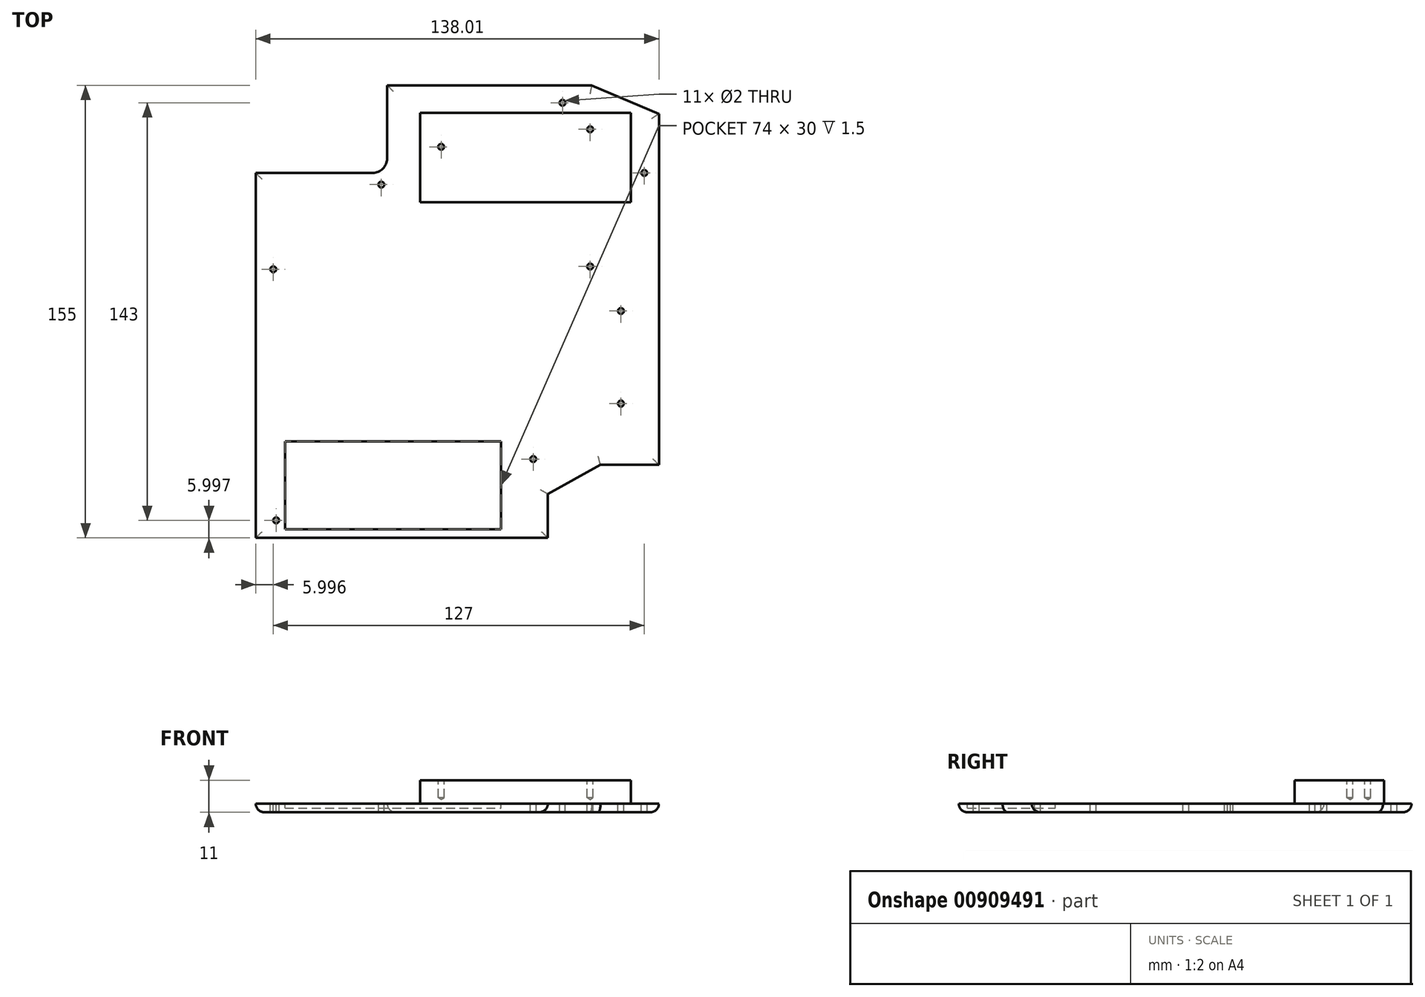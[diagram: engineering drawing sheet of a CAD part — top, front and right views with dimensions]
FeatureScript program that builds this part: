
annotation { "Feature Type Name" : "Feature", "Feature Type Description" : "" }
export const myFeature = defineFeature(function(context is Context, id is Id, definition is map)
    precondition{}
    {
        {
            var Q0;
            Q0=qCreatedBy(makeId("Top.planeOp"),FACE);
            var sketch = newSketch(context, id + "F0", { "sketchPlane" : qUnion([Q0])});
            skLineSegment(sketch, "E0.bottom", {"start": v(-71.65, 50.25) * mm, "end": v(-26.65, 50.25) * mm});
            skLineSegment(sketch, "E0.top", {"start": v(-71.65, -74.75) * mm, "end": v(-26.65, -74.75) * mm});
            skLineSegment(sketch, "E0.left", {"start": v(-71.65, 50.25) * mm, "end": v(-71.65, -74.75) * mm});
            skLineSegment(sketch, "E0.right", {"start": v(-26.65, 50.25) * mm, "end": v(-26.65, -74.75) * mm});
            skLineSegment(sketch, "E1.bottom", {"start": v(-26.65, 50.25) * mm, "end": v(43.35, 50.25) * mm});
            skLineSegment(sketch, "E1.top", {"start": v(-26.65, 80.25) * mm, "end": v(43.35, 80.25) * mm});
            skLineSegment(sketch, "E1.left", {"start": v(-26.65, 50.25) * mm, "end": v(-26.65, 80.25) * mm});
            skLineSegment(sketch, "E1.right", {"start": v(43.35, 50.25) * mm, "end": v(43.35, 80.25) * mm});
            skLineSegment(sketch, "E2", {"start": v(43.35, 80.25) * mm, "end": v(66.36, 70.48) * mm});
            skLineSegment(sketch, "E3.bottom", {"start": v(66.36, 70.48) * mm, "end": v(43.35, 70.48) * mm});
            skLineSegment(sketch, "E3.top", {"start": v(66.36, 50.25) * mm, "end": v(43.35, 50.25) * mm});
            skLineSegment(sketch, "E3.left", {"start": v(66.36, 70.48) * mm, "end": v(66.36, 50.25) * mm});
            skLineSegment(sketch, "E3.right", {"start": v(43.35, 70.48) * mm, "end": v(43.35, 50.25) * mm});
            skLineSegment(sketch, "E4.bottom", {"start": v(66.36, 50.25) * mm, "end": v(46.36, 50.25) * mm});
            skLineSegment(sketch, "E4.top", {"start": v(66.36, -49.75) * mm, "end": v(46.36, -49.75) * mm});
            skLineSegment(sketch, "E4.left", {"start": v(66.36, 50.25) * mm, "end": v(66.36, -49.75) * mm});
            skLineSegment(sketch, "E4.right", {"start": v(46.36, 50.25) * mm, "end": v(46.36, -49.75) * mm});
            skLineSegment(sketch, "E5.bottom", {"start": v(-71.65, -74.75) * mm, "end": v(28.35, -74.75) * mm});
            skLineSegment(sketch, "E5.top", {"start": v(-71.65, -59.75) * mm, "end": v(28.35, -59.75) * mm});
            skLineSegment(sketch, "E5.left", {"start": v(-71.65, -74.75) * mm, "end": v(-71.65, -59.75) * mm});
            skLineSegment(sketch, "E5.right", {"start": v(28.35, -74.75) * mm, "end": v(28.35, -59.75) * mm});
            skLineSegment(sketch, "E6", {"start": v(28.35, -59.75) * mm, "end": v(46.36, -49.75) * mm});
            skSolve(sketch);
        }
        {
            var Q0;
            {var subQ0=sQuery(id+"F0.wireOp",EDGE,"E0.bottom");Q0=makeQuery(id+"F0.imprint","IMPRINT",FACE,{"disambiguationData":[TD([[makeQuery(id+"F0.imprint","IMPRINT",EDGE,{"derivedFrom":subQ0}),-1.0]])]});}
            var Q1;
            {var subQ1=sQuery(id+"F0.wireOp",EDGE,"E1.bottom");Q1=makeQuery(id+"F0.imprint","IMPRINT",FACE,{"disambiguationData":[TD([[makeQuery(id+"F0.imprint","IMPRINT",EDGE,{"derivedFrom":subQ1}),-1.0]])]});}
            var Q2;
            {var subQ0=sQuery(id+"F0.wireOp",EDGE,"E0.top");Q2=makeQuery(id+"F0.imprint","IMPRINT",FACE,{"disambiguationData":[TD([[makeQuery(id+"F0.imprint","IMPRINT",EDGE,{"derivedFrom":subQ0}),1.0]])]});}
            var Q3;
            Q3=makeQuery(id+"F0.imprint","IMPRINT",FACE,{"disambiguationData":[TD([[makeQuery(id+"F0.imprint","IMPRINT",EDGE,{"derivedFrom":sQuery(id+"F0.wireOp",EDGE,"E4.top")}),-1.0]])]});
            var Q4;
            {var subQ0=sQuery(id+"F0.wireOp",EDGE,"E5.bottom");Q4=makeQuery(id+"F0.imprint","IMPRINT",FACE,{"disambiguationData":[TD([[makeQuery(id+"F0.imprint","IMPRINT",EDGE,{"derivedFrom":subQ0}),1.0]])]});}
            var Q5;
            {var subQ1=sQuery(id+"F0.wireOp",EDGE,"E1.bottom");Q5=makeQuery(id+"F0.imprint","IMPRINT",FACE,{"disambiguationData":[TD([[makeQuery(id+"F0.imprint","IMPRINT",EDGE,{"derivedFrom":subQ1}),1.0]])]});}
            var Q6;
            {var subQ3=sQuery(id+"F0.wireOp",EDGE,"E3.bottom");Q6=makeQuery(id+"F0.imprint","IMPRINT",FACE,{"disambiguationData":[TD([[makeQuery(id+"F0.imprint","IMPRINT",EDGE,{"derivedFrom":subQ3}),1.0]])]});}
            var Q7;
            {var subQ0=sQuery(id+"F0.wireOp",EDGE,"E2");Q7=makeQuery(id+"F0.imprint","IMPRINT",FACE,{"disambiguationData":[TD([[makeQuery(id+"F0.imprint","IMPRINT",EDGE,{"derivedFrom":subQ0}),-1.0]])]});}
            extrude(context, id + "F1", {"entities" : qUnion([Q0, Q1, Q2, Q3, Q4, Q5, Q6, Q7]), "depth" : 3 * mm, "offsetDistance" : 25 * mm});
        }
        {
            var Q0;
            Q0=makeQuery(id+"F1.opExtrude","SWEPT_EDGE",EDGE,{"disambiguationData":[OSD([sQuery(id+"F0.wireOp",EDGE,"E0.bottom"),sQuery(id+"F0.wireOp",EDGE,"E0.right"),sQuery(id+"F0.wireOp",EDGE,"E1.bottom"),sQuery(id+"F0.wireOp",EDGE,"E1.left")])]});
            fillet(context, id + "F2", {"entities" : qUnion([Q0]), "radius" : 5 * mm, "tangentPropagation" : true, "allowEdgeOverflow" : false});
        }
        {
            var Q0;
            Q0=makeQuery(id+"F1.opExtrude","CAP_FACE",FACE,{"disambiguationData":[OSD([sQuery(id+"F0.wireOp",EDGE,"E0.bottom"),sQuery(id+"F0.wireOp",EDGE,"E0.top"),sQuery(id+"F0.wireOp",EDGE,"E0.left"),sQuery(id+"F0.wireOp",EDGE,"E1.top"),sQuery(id+"F0.wireOp",EDGE,"E1.left"),sQuery(id+"F0.wireOp",EDGE,"E2"),sQuery(id+"F0.wireOp",EDGE,"E3.left"),sQuery(id+"F0.wireOp",EDGE,"E4.top"),sQuery(id+"F0.wireOp",EDGE,"E4.left"),sQuery(id+"F0.wireOp",EDGE,"E5.bottom"),sQuery(id+"F0.wireOp",EDGE,"E5.right"),sQuery(id+"F0.wireOp",EDGE,"E6")])],"isStart":true});
            fillet(context, id + "F3", {"entities" : qUnion([Q0]), "radius" : 3 * mm, "tangentPropagation" : true, "allowEdgeOverflow" : false});
        }
        {
            var Q0;
            Q0=makeQuery(id+"F1.opExtrude","CAP_FACE",FACE,{"disambiguationData":[OSD([sQuery(id+"F0.wireOp",EDGE,"E0.bottom"),sQuery(id+"F0.wireOp",EDGE,"E0.top"),sQuery(id+"F0.wireOp",EDGE,"E0.left"),sQuery(id+"F0.wireOp",EDGE,"E1.top"),sQuery(id+"F0.wireOp",EDGE,"E1.left"),sQuery(id+"F0.wireOp",EDGE,"E2"),sQuery(id+"F0.wireOp",EDGE,"E3.left"),sQuery(id+"F0.wireOp",EDGE,"E4.top"),sQuery(id+"F0.wireOp",EDGE,"E4.left"),sQuery(id+"F0.wireOp",EDGE,"E5.bottom"),sQuery(id+"F0.wireOp",EDGE,"E5.right"),sQuery(id+"F0.wireOp",EDGE,"E6")])],"isStart":false});
            var sketch = newSketch(context, id + "F4", { "sketchPlane" : qUnion([Q0])});
            skPoint(sketch, "E7", {"position": v(-64.65, -68.75) * mm});
            skPoint(sketch, "E8", {"position": v(-65.65, 17.25) * mm});
            skPoint(sketch, "E9", {"position": v(-28.65, 46.25) * mm});
            skPoint(sketch, "E10", {"position": v(33.35, 74.25) * mm});
            skPoint(sketch, "E11", {"position": v(61.35, 50.25) * mm});
            skPoint(sketch, "E12", {"position": v(23.35, -47.75) * mm});
            skPoint(sketch, "E13", {"position": v(53.36, -28.75) * mm});
            skPoint(sketch, "E14", {"position": v(53.36, 2.97) * mm});
            skSolve(sketch);
        }
        {
            var Q0;
            Q0=sQuery(id+"F4.wireOp",VERTEX,"E8");
            var Q1;
            Q1=sQuery(id+"F4.wireOp",VERTEX,"E7");
            var Q2;
            Q2=sQuery(id+"F4.wireOp",VERTEX,"E12");
            var Q3;
            Q3=sQuery(id+"F4.wireOp",VERTEX,"E13");
            var Q4;
            Q4=sQuery(id+"F4.wireOp",VERTEX,"E14");
            var Q5;
            Q5=sQuery(id+"F4.wireOp",VERTEX,"E11");
            var Q6;
            Q6=sQuery(id+"F4.wireOp",VERTEX,"E10");
            var Q7;
            Q7=sQuery(id+"F4.wireOp",VERTEX,"E9");
            var Q8;
            Q8=makeQuery(id+"F1.opExtrude","SWEPT_BODY",BODY,{"disambiguationData":[OSD([sQuery(id+"F0.wireOp",EDGE,"E0.bottom"),sQuery(id+"F0.wireOp",EDGE,"E0.top"),sQuery(id+"F0.wireOp",EDGE,"E0.left"),sQuery(id+"F0.wireOp",EDGE,"E1.top"),sQuery(id+"F0.wireOp",EDGE,"E1.left"),sQuery(id+"F0.wireOp",EDGE,"E2"),sQuery(id+"F0.wireOp",EDGE,"E3.left"),sQuery(id+"F0.wireOp",EDGE,"E4.top"),sQuery(id+"F0.wireOp",EDGE,"E4.left"),sQuery(id+"F0.wireOp",EDGE,"E5.bottom"),sQuery(id+"F0.wireOp",EDGE,"E5.right"),sQuery(id+"F0.wireOp",EDGE,"E6")])]});
            hole(context, id + "F5", {"style" : HoleStyle.SIMPLE, "endStyle" : HoleEndStyle.THROUGH, "holeDiameter" : 2 * mm, "majorDiameter" : 5 * mm, "isTappedThrough" : true, "tappedDepth" : 12 * mm, "tapClearance" : 3, "locations" : qUnion([Q0, Q1, Q2, Q3, Q4, Q5, Q6, Q7]), "scope" : qUnion([Q8])});
        }
        {
            var Q0;
            Q0=makeQuery(id+"F1.opExtrude","CAP_FACE",FACE,{"disambiguationData":[OSD([sQuery(id+"F0.wireOp",EDGE,"E0.bottom"),sQuery(id+"F0.wireOp",EDGE,"E0.top"),sQuery(id+"F0.wireOp",EDGE,"E0.left"),sQuery(id+"F0.wireOp",EDGE,"E1.top"),sQuery(id+"F0.wireOp",EDGE,"E1.left"),sQuery(id+"F0.wireOp",EDGE,"E2"),sQuery(id+"F0.wireOp",EDGE,"E3.left"),sQuery(id+"F0.wireOp",EDGE,"E4.top"),sQuery(id+"F0.wireOp",EDGE,"E4.left"),sQuery(id+"F0.wireOp",EDGE,"E5.bottom"),sQuery(id+"F0.wireOp",EDGE,"E5.right"),sQuery(id+"F0.wireOp",EDGE,"E6")])],"isStart":false});
            var sketch = newSketch(context, id + "F6", { "sketchPlane" : qUnion([Q0])});
            skLineSegment(sketch, "E15.bottom", {"start": v(-61.65, -71.75) * mm, "end": v(12.35, -71.75) * mm});
            skLineSegment(sketch, "E15.top", {"start": v(-61.65, -41.75) * mm, "end": v(12.35, -41.75) * mm});
            skLineSegment(sketch, "E15.left", {"start": v(-61.65, -71.75) * mm, "end": v(-61.65, -41.75) * mm});
            skLineSegment(sketch, "E15.right", {"start": v(12.35, -71.75) * mm, "end": v(12.35, -41.75) * mm});
            skLineSegment(sketch, "E16.bottom", {"start": v(-59.65, -41.75) * mm, "end": v(10.35, -41.75) * mm});
            skLineSegment(sketch, "E16.top", {"start": v(-59.65, 40.25) * mm, "end": v(10.35, 40.25) * mm});
            skLineSegment(sketch, "E16.left", {"start": v(-59.65, -41.75) * mm, "end": v(-59.65, 40.25) * mm});
            skLineSegment(sketch, "E16.right", {"start": v(10.35, -41.75) * mm, "end": v(10.35, 40.25) * mm});
            skSolve(sketch);
        }
        {
            var Q0;
            Q0=makeQuery(id+"F6.imprint","IMPRINT",FACE,{"disambiguationData":[TD([[makeQuery(id+"F6.imprint","IMPRINT",EDGE,{"derivedFrom":sQuery(id+"F6.wireOp",EDGE,"E16.bottom")}),1.0]])]});
            var Q1;
            Q1=makeQuery(id+"F6.imprint","IMPRINT",FACE,{"disambiguationData":[TD([[makeQuery(id+"F6.imprint","IMPRINT",EDGE,{"derivedFrom":sQuery(id+"F6.wireOp",EDGE,"E15.bottom")}),1.0]])]});
            extrude(context, id + "F7", {"entities" : qUnion([Q0, Q1]), "operationType" : NewBodyOperationType.REMOVE, "oppositeDirection" : true, "depth" : 1.5 * mm, "offsetDistance" : 25 * mm});
        }
        {
            var Q0;
            Q0=makeQuery(id+"F1.opExtrude","CAP_FACE",FACE,{"disambiguationData":[OSD([sQuery(id+"F0.wireOp",EDGE,"E0.bottom"),sQuery(id+"F0.wireOp",EDGE,"E0.top"),sQuery(id+"F0.wireOp",EDGE,"E0.left"),sQuery(id+"F0.wireOp",EDGE,"E1.top"),sQuery(id+"F0.wireOp",EDGE,"E1.left"),sQuery(id+"F0.wireOp",EDGE,"E2"),sQuery(id+"F0.wireOp",EDGE,"E3.left"),sQuery(id+"F0.wireOp",EDGE,"E4.top"),sQuery(id+"F0.wireOp",EDGE,"E4.left"),sQuery(id+"F0.wireOp",EDGE,"E5.bottom"),sQuery(id+"F0.wireOp",EDGE,"E5.right"),sQuery(id+"F0.wireOp",EDGE,"E6")])],"isStart":false});
            var sketch = newSketch(context, id + "F8", { "sketchPlane" : qUnion([Q0])});
            skLineSegment(sketch, "E17.bottom", {"start": v(-15.39, 40.25) * mm, "end": v(56.71, 40.25) * mm});
            skLineSegment(sketch, "E17.top", {"start": v(-15.39, 70.88) * mm, "end": v(56.71, 70.88) * mm});
            skLineSegment(sketch, "E17.left", {"start": v(-15.39, 40.25) * mm, "end": v(-15.39, 70.88) * mm});
            skLineSegment(sketch, "E17.right", {"start": v(56.71, 40.25) * mm, "end": v(56.71, 70.88) * mm});
            skLineSegment(sketch, "E18.bottom", {"start": v(56.71, 40.25) * mm, "end": v(10.35, 40.25) * mm});
            skLineSegment(sketch, "E18.top", {"start": v(56.71, 14.74) * mm, "end": v(10.35, 14.74) * mm});
            skLineSegment(sketch, "E18.left", {"start": v(56.71, 40.25) * mm, "end": v(56.71, 14.74) * mm});
            skLineSegment(sketch, "E18.right", {"start": v(10.35, 40.25) * mm, "end": v(10.35, 14.74) * mm});
            skSolve(sketch);
        }
        {
            var Q0;
            Q0=makeQuery(id+"F8.imprint","IMPRINT",FACE,{"disambiguationData":[TD([[makeQuery(id+"F8.imprint","IMPRINT",EDGE,{"derivedFrom":sQuery(id+"F8.wireOp",EDGE,"E17.bottom")}),1.0]])]});
            var Q1;
            Q1=makeQuery(id+"F8.imprint","IMPRINT",FACE,{"disambiguationData":[TD([[makeQuery(id+"F8.imprint","IMPRINT",EDGE,{"derivedFrom":sQuery(id+"F8.wireOp",EDGE,"E18.bottom")}),1.0]])]});
            extrude(context, id + "F9", {"entities" : qUnion([Q0, Q1]), "operationType" : NewBodyOperationType.ADD, "depth" : 8 * mm, "offsetDistance" : 25 * mm});
        }
        {
            var Q0;
            Q0=makeQuery(id+"F9.opExtrude","CAP_FACE",FACE,{"disambiguationData":[OSD([sQuery(id+"F8.wireOp",EDGE,"E17.bottom"),sQuery(id+"F8.wireOp",EDGE,"E17.top"),sQuery(id+"F8.wireOp",EDGE,"E17.left"),sQuery(id+"F8.wireOp",EDGE,"E17.right"),sQuery(id+"F8.wireOp",EDGE,"E18.top"),sQuery(id+"F8.wireOp",EDGE,"E18.left"),sQuery(id+"F8.wireOp",EDGE,"E18.right")])],"isStart":false});
            var sketch = newSketch(context, id + "F10", { "sketchPlane" : qUnion([Q0])});
            skPoint(sketch, "E19", {"position": v(-8.18, 59.19) * mm});
            skPoint(sketch, "E20", {"position": v(42.82, 65.19) * mm});
            skPoint(sketch, "E21", {"position": v(42.82, 18.19) * mm});
            skSolve(sketch);
        }
        {
            var Q0;
            Q0=sQuery(id+"F10.wireOp",VERTEX,"E19");
            var Q1;
            Q1=sQuery(id+"F10.wireOp",VERTEX,"E20");
            var Q2;
            Q2=sQuery(id+"F10.wireOp",VERTEX,"E21");
            var Q3;
            Q3=makeQuery(id+"F1.opExtrude","SWEPT_BODY",BODY,{"disambiguationData":[OSD([sQuery(id+"F0.wireOp",EDGE,"E0.bottom"),sQuery(id+"F0.wireOp",EDGE,"E0.top"),sQuery(id+"F0.wireOp",EDGE,"E0.left"),sQuery(id+"F0.wireOp",EDGE,"E1.top"),sQuery(id+"F0.wireOp",EDGE,"E1.left"),sQuery(id+"F0.wireOp",EDGE,"E2"),sQuery(id+"F0.wireOp",EDGE,"E3.left"),sQuery(id+"F0.wireOp",EDGE,"E4.top"),sQuery(id+"F0.wireOp",EDGE,"E4.left"),sQuery(id+"F0.wireOp",EDGE,"E5.bottom"),sQuery(id+"F0.wireOp",EDGE,"E5.right"),sQuery(id+"F0.wireOp",EDGE,"E6")])]});
            hole(context, id + "F11", {"style" : HoleStyle.SIMPLE, "endStyle" : HoleEndStyle.BLIND, "holeDiameter" : 2 * mm, "majorDiameter" : 5 * mm, "holeDepth" : 6 * mm, "isTappedThrough" : true, "tappedDepth" : 12 * mm, "tapClearance" : 3, "locations" : qUnion([Q0, Q1, Q2]), "scope" : qUnion([Q3])});
        }
    });
